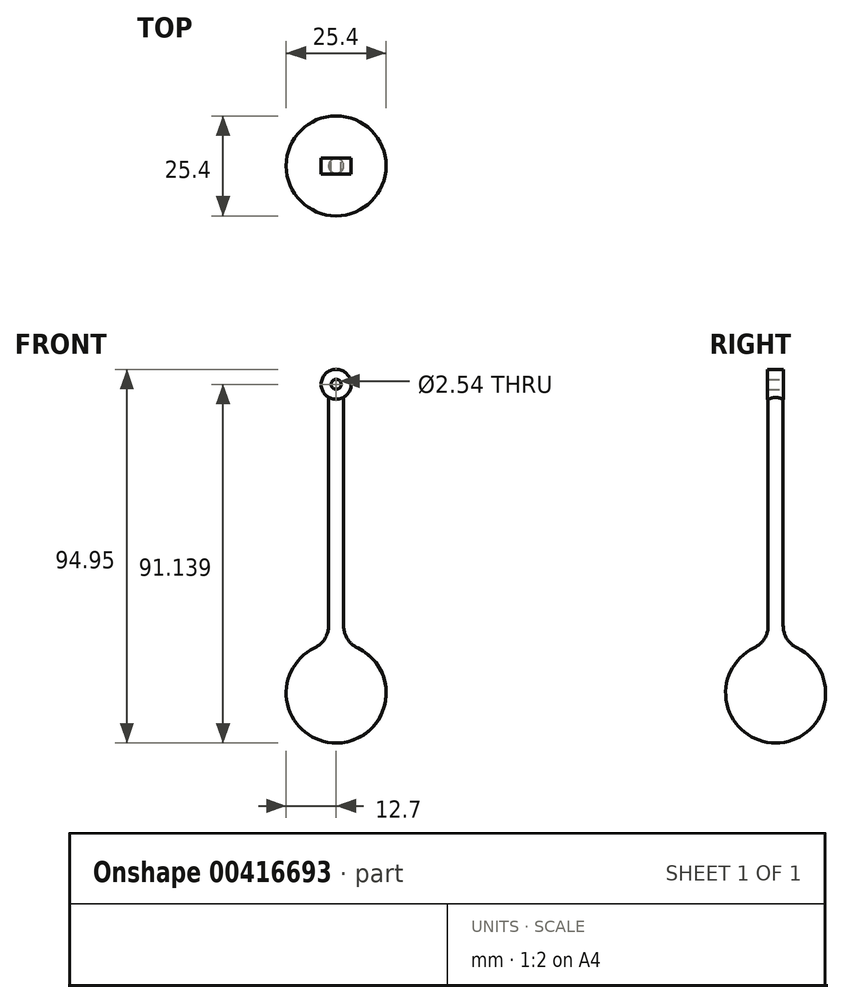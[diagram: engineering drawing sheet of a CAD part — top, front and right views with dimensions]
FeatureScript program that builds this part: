
annotation { "Feature Type Name" : "Feature", "Feature Type Description" : "" }
export const myFeature = defineFeature(function(context is Context, id is Id, definition is map)
    precondition{}
    {
        {
            var Q0;
            Q0=qCreatedBy(makeId("Front.planeOp"),FACE);
            var sketch = newSketch(context, id + "F0", { "sketchPlane" : qUnion([Q0])});
            skArc(sketch, "E0", {"start": v(0, -88.76) * mm, "mid": v(12.38, -78.88) * mm, "end": v(5.5, -64.61) * mm});
            skLineSegment(sketch, "E1", {"start": v(1.9, 0) * mm, "end": v(1.9, -58.89) * mm});
            skLineSegment(sketch, "E2", {"start": v(0, -88.76) * mm, "end": v(0, 0) * mm});
            skLineSegment(sketch, "E3", {"start": v(1.9, 0) * mm, "end": v(0, 0) * mm});
            skPoint(sketch, "E4.orphan", {"position": v(0, -68.68) * mm});
            skPoint(sketch, "E5.visualSharp", {"position": v(1.9, -63.5) * mm});
            skArc(sketch, "E5.filletArc", {"start": v(1.9, -58.89) * mm, "mid": v(2.88, -62.27) * mm, "end": v(5.5, -64.61) * mm});
            skSolve(sketch);
        }
        {
            var Q0;
            Q0=makeQuery(id+"F0.imprint","IMPRINT",FACE,{"disambiguationData":[TD([[makeQuery(id+"F0.imprint","IMPRINT",EDGE,{"derivedFrom":sQuery(id+"F0.wireOp",EDGE,"E0")}),1.0]])]});
            var Q1;
            Q1=sQuery(id+"F0.wireOp",EDGE,"E2");
            revolve(context, id + "F1", {"entities" : qUnion([Q0]), "axis" : qUnion([Q1]), "revolveType" : RevolveType.FULL});
        }
        {
            var Q0;
            Q0=qCreatedBy(makeId("Front.planeOp"),FACE);
            var sketch = newSketch(context, id + "F2", { "sketchPlane" : qUnion([Q0])});
            skCircle(sketch, "E6", {"center": v(0, 2.38) * mm, "radius": 1.27 * mm});
            skCircle(sketch, "E7", {"center": v(0, 2.38) * mm, "radius": 3.81 * mm});
            skSolve(sketch);
        }
        {
            var Q0;
            Q0=makeQuery(id+"F2.imprint","IMPRINT",FACE,{"disambiguationData":[TD([[makeQuery(id+"F2.imprint","IMPRINT",EDGE,{"derivedFrom":sQuery(id+"F2.wireOp",EDGE,"E6")}),-1.0]])]});
            extrude(context, id + "F3", {"entities" : qUnion([Q0]), "operationType" : NewBodyOperationType.ADD, "depth" : 2.03 * mm, "hasSecondDirection" : true, "secondDirectionOppositeDirection" : true, "secondDirectionDepth" : 2.03 * mm});
        }
    });
